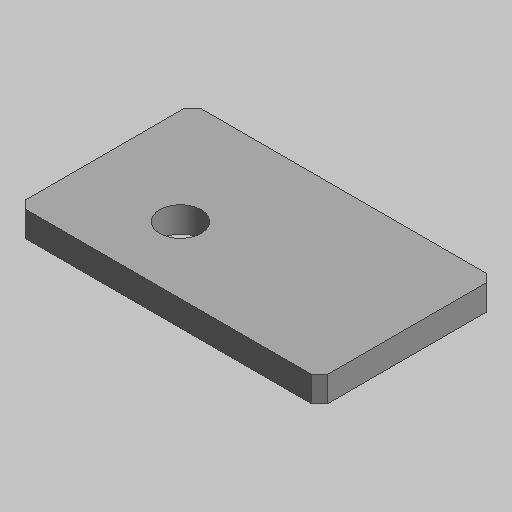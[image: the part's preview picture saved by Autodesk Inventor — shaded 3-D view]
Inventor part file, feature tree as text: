
AUTODESK INVENTOR PART (.ipt)
format: ipt  version: 2023.5 (Build 275446000, 446)  size: 54,784 bytes
history: native  units: mm (DEFAULTED — no unit token found)
features: chamfer x1
ambient origin geometry x8: Origin, YZ Plane, XZ Plane, XY Plane, X Axis, Y Axis, Z Axis, Center Point
bodies: Solid1 (feature_tree)
feature tree (1):
  chamfer  "Chamfer1"  [1 undecoded]
note: 1 required parameter value undecoded (feature->parameter linkage not recoverable at this tier; creation-order binding heuristic only, values carry confidence <= 0.55)
